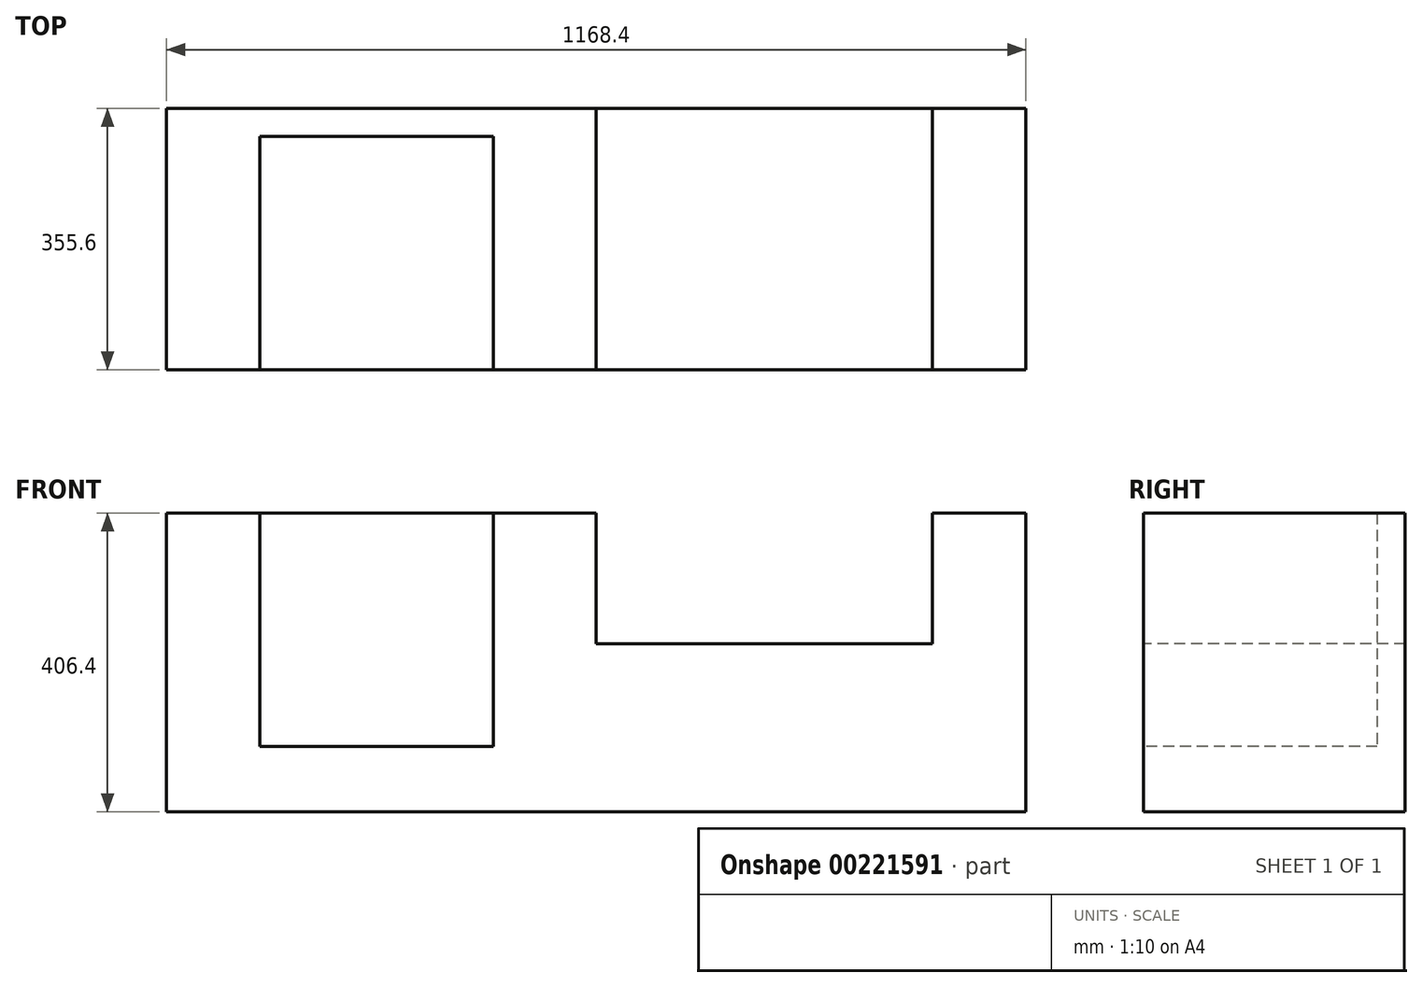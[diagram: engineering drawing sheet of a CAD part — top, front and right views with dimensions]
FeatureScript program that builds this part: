
annotation { "Feature Type Name" : "Feature", "Feature Type Description" : "" }
export const myFeature = defineFeature(function(context is Context, id is Id, definition is map)
    precondition{}
    {
        {
            var Q0;
            Q0=qCreatedBy(makeId("Top.planeOp"),FACE);
            var sketch = newSketch(context, id + "F0", { "sketchPlane" : qUnion([Q0])});
            skLineSegment(sketch, "E0", {"start": v(-598.84, 125.57) * mm, "end": v(569.56, 125.57) * mm});
            skLineSegment(sketch, "E1", {"start": v(569.56, 125.57) * mm, "end": v(569.56, -230.03) * mm});
            skLineSegment(sketch, "E2", {"start": v(569.56, -230.03) * mm, "end": v(-598.84, -230.03) * mm});
            skLineSegment(sketch, "E3", {"start": v(-598.84, -230.03) * mm, "end": v(-598.84, 125.57) * mm});
            skSolve(sketch);
        }
        {
            var Q0;
            Q0 = qSketchRegion(id + "F0", true);
            var Q1;
            Q1=makeQuery(id+"F0.imprint","IMPRINT",FACE,{"disambiguationData":[TD([[makeQuery(id+"F0.imprint","IMPRINT",EDGE,{"derivedFrom":sQuery(id+"F0.wireOp",EDGE,"E0")}),-1.0]])]});
            extrude(context, id + "F1", {"entities" : qUnion([Q0, Q1]), "depth" : 406.4 * mm});
        }
        {
            var Q0;
            Q0=makeQuery(id+"F1.opExtrude","SWEPT_FACE",FACE,{"disambiguationData":[OSD([sQuery(id+"F0.wireOp",EDGE,"E2")])]});
            var sketch = newSketch(context, id + "F2", { "sketchPlane" : qUnion([Q0])});
            skLineSegment(sketch, "E4", {"start": v(-471.84, 406.4) * mm, "end": v(-471.84, 88.9) * mm});
            skLineSegment(sketch, "E5", {"start": v(-471.84, 88.9) * mm, "end": v(-154.34, 88.9) * mm});
            skLineSegment(sketch, "E6", {"start": v(-154.34, 88.9) * mm, "end": v(-154.34, 406.4) * mm});
            skLineSegment(sketch, "E7", {"start": v(-14.64, 406.4) * mm, "end": v(-14.64, 228.6) * mm});
            skLineSegment(sketch, "E8", {"start": v(-14.64, 228.6) * mm, "end": v(442.56, 228.6) * mm});
            skLineSegment(sketch, "E9", {"start": v(442.56, 228.6) * mm, "end": v(442.56, 406.4) * mm});
            skSolve(sketch);
        }
        {
            var Q0;
            Q0 = qSketchRegion(id + "F2", true);
            var Q1;
            {var subQ0=sQuery(id+"F2.wireOp",EDGE,"E7");Q1=makeQuery(id+"F2.imprint","IMPRINT",FACE,{"disambiguationData":[TD([[makeQuery(id+"F2.imprint","IMPRINT",EDGE,{"derivedFrom":subQ0}),1.0]])]});}
            extrude(context, id + "F3", {"entities" : qUnion([Q0, Q1]), "operationType" : NewBodyOperationType.REMOVE, "oppositeDirection" : true, "depth" : 355.6 * mm});
        }
        {
            var Q0;
            {var subQ0=sQuery(id+"F2.wireOp",EDGE,"E4");Q0=makeQuery(id+"F2.imprint","IMPRINT",FACE,{"disambiguationData":[TD([[makeQuery(id+"F2.imprint","IMPRINT",EDGE,{"derivedFrom":subQ0}),1.0]])]});}
            extrude(context, id + "F4", {"entities" : qUnion([Q0]), "operationType" : NewBodyOperationType.REMOVE, "oppositeDirection" : true, "depth" : 317.5 * mm});
        }
    });
